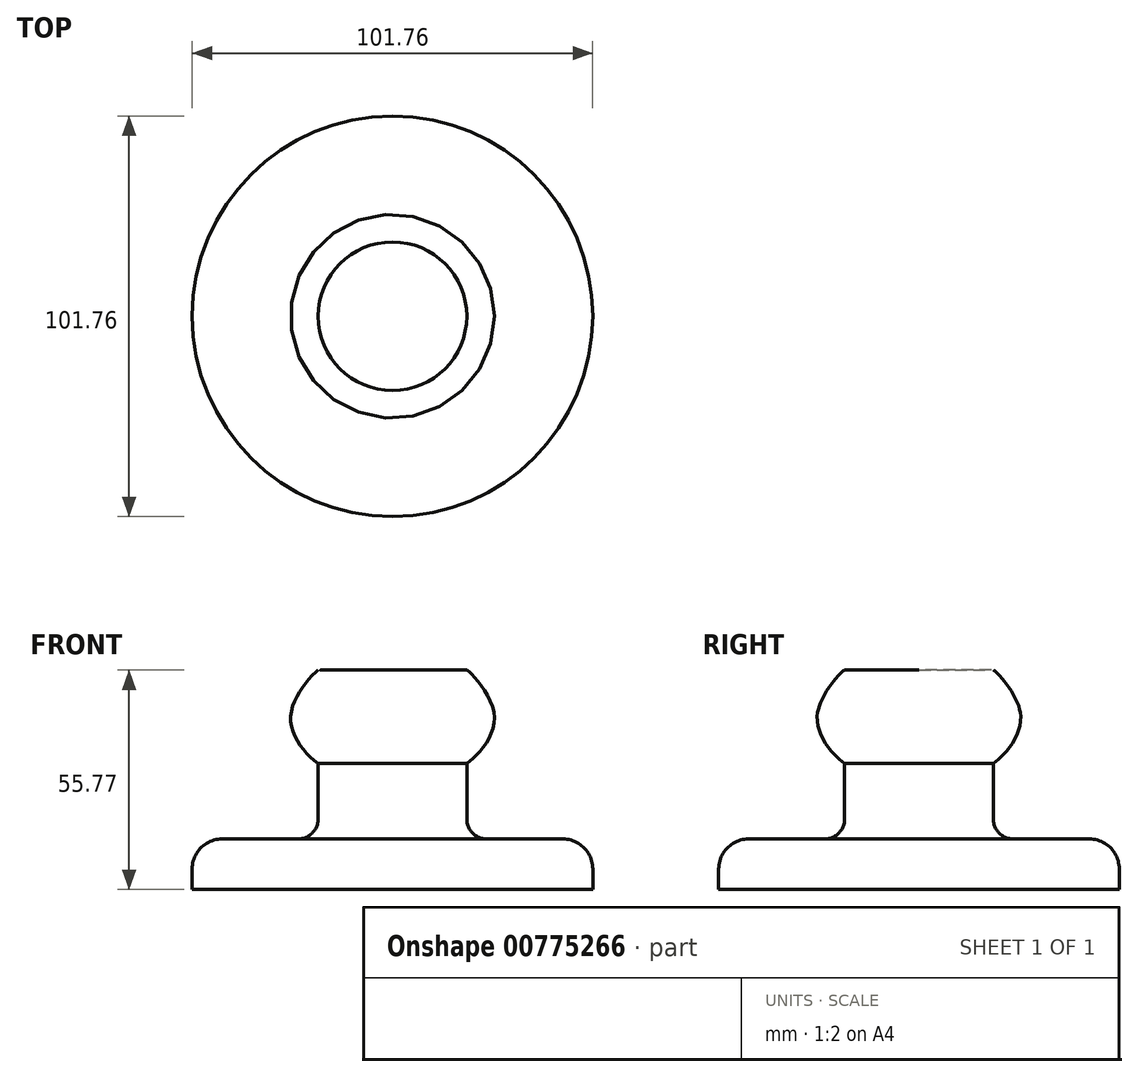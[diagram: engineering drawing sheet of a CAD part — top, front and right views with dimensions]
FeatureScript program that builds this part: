
annotation { "Feature Type Name" : "Feature", "Feature Type Description" : "" }
export const myFeature = defineFeature(function(context is Context, id is Id, definition is map)
    precondition{}
    {
        {
            var Q0;
            Q0=qCreatedBy(makeId("Front.planeOp"),FACE);
            var sketch = newSketch(context, id + "F0", { "sketchPlane" : qUnion([Q0])});
            skLineSegment(sketch, "E0", {"start": v(0, 0) * mm, "end": v(50.88, 0) * mm});
            skLineSegment(sketch, "E1", {"start": v(50.88, 0) * mm, "end": v(50.88, 12.84) * mm});
            skLineSegment(sketch, "E2", {"start": v(50.88, 12.84) * mm, "end": v(18.88, 12.84) * mm});
            skLineSegment(sketch, "E3", {"start": v(18.88, 12.84) * mm, "end": v(18.88, 32) * mm});
            skFitSpline(sketch, "E4", {"points": [v(18.88, 32) * mm, v(25.78, 44.84) * mm, v(18.88, 55.77) * mm, v(18.88, 55.58) * mm], "startDerivative": vector(18.64, 13.82) * mm, "endDerivative": vector(0.86, -5.29) * mm});
            skLineSegment(sketch, "E5", {"start": v(18.88, 55.77) * mm, "end": v(0, 55.77) * mm});
            skLineSegment(sketch, "E6", {"start": v(0, 55.77) * mm, "end": v(0, 0) * mm});
            skSolve(sketch);
        }
        {
            var Q0;
            Q0=makeQuery(id+"F0.imprint","IMPRINT",FACE,{"disambiguationData":[TD([[makeQuery(id+"F0.imprint","IMPRINT",EDGE,{"derivedFrom":sQuery(id+"F0.wireOp",EDGE,"E0")}),1.0]])]});
            var Q1;
            Q1=sQuery(id+"F0.wireOp",EDGE,"E6");
            revolve(context, id + "F1", {"surfaceOperationType" : NewSurfaceOperationType.NEW, "entities" : qUnion([Q0]), "axis" : qUnion([Q1]), "revolveType" : RevolveType.FULL});
        }
        {
            var Q0;
            Q0=makeQuery(id+"F1.opRevolve","SWEPT_EDGE",EDGE,{"disambiguationData":[OSD([sQuery(id+"F0.wireOp",EDGE,"E2"),sQuery(id+"F0.wireOp",EDGE,"E3")])]});
            fillet(context, id + "F2", {"entities" : qUnion([Q0]), "radius" : 5.08 * mm, "tangentPropagation" : true, "allowEdgeOverflow" : false});
        }
        {
            var Q0;
            Q0=makeQuery(id+"F1.opRevolve","SWEPT_EDGE",EDGE,{"disambiguationData":[OSD([sQuery(id+"F0.wireOp",EDGE,"E1"),sQuery(id+"F0.wireOp",EDGE,"E2")])]});
            fillet(context, id + "F3", {"entities" : qUnion([Q0]), "radius" : 7.62 * mm, "tangentPropagation" : true, "allowEdgeOverflow" : false});
        }
        {
            var Q0;
            Q0=qCreatedBy(makeId("Top.planeOp"),FACE);
            var sketch = newSketch(context, id + "F4", { "sketchPlane" : qUnion([Q0])});
            skCircle(sketch, "E7", {"center": v(0, 0) * mm, "radius": 14.29 * mm});
            skSolve(sketch);
        }
        {
            var Q0;
            Q0=makeQuery(id+"F4.imprint","IMPRINT",FACE,{"disambiguationData":[TD([[makeQuery(id+"F4.imprint","IMPRINT",EDGE,{"derivedFrom":sQuery(id+"F4.wireOp",EDGE,"E7")}),1.0]])]});
            var Q1;
            Q1=sQuery(id+"F4.wireOp",EDGE,"E7");
            extrude(context, id + "F5", {"entities" : qUnion([Q0]), "operationType" : NewBodyOperationType.ADD, "surfaceEntities" : qUnion([Q1]), "depth" : 25.4 * mm, "offsetDistance" : 25.4 * mm});
        }
    });
